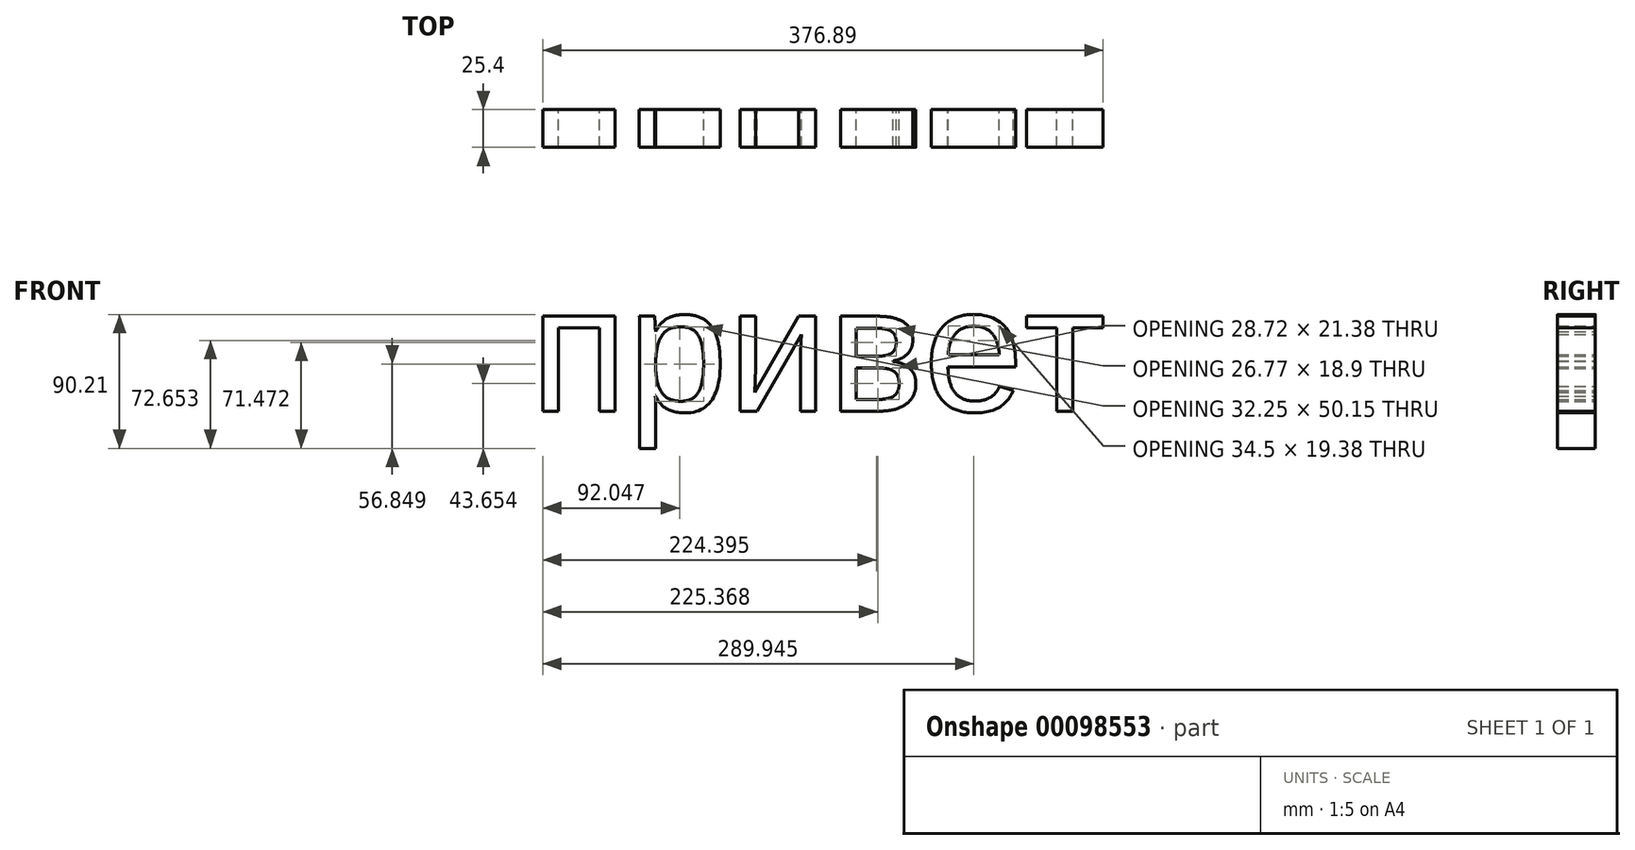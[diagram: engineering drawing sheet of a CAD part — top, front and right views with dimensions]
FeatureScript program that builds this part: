
annotation { "Feature Type Name" : "Feature", "Feature Type Description" : "" }
export const myFeature = defineFeature(function(context is Context, id is Id, definition is map)
    precondition{}
    {
        {
            var Q0;
            Q0=qCreatedBy(makeId("Front.planeOp"),FACE);
            var sketch = newSketch(context, id + "F0", { "sketchPlane" : qUnion([Q0])});
            skText(sketch, "E0", { "text": "привет", "fontName": "Arimo-Regular.ttf"});
            const initialGuessF0  = {"E0": [-0.05514, -0.05719, 1, 0, 0.08711]};
            skSetInitialGuess(sketch, initialGuessF0);
            skSolve(sketch);
        }
        {
            var Q0;
            Q0 = qSketchRegion(id + "F0", true);
            extrude(context, id + "F1", {"entities" : qUnion([Q0]), "depth" : 25.4 * mm});
        }
    });
